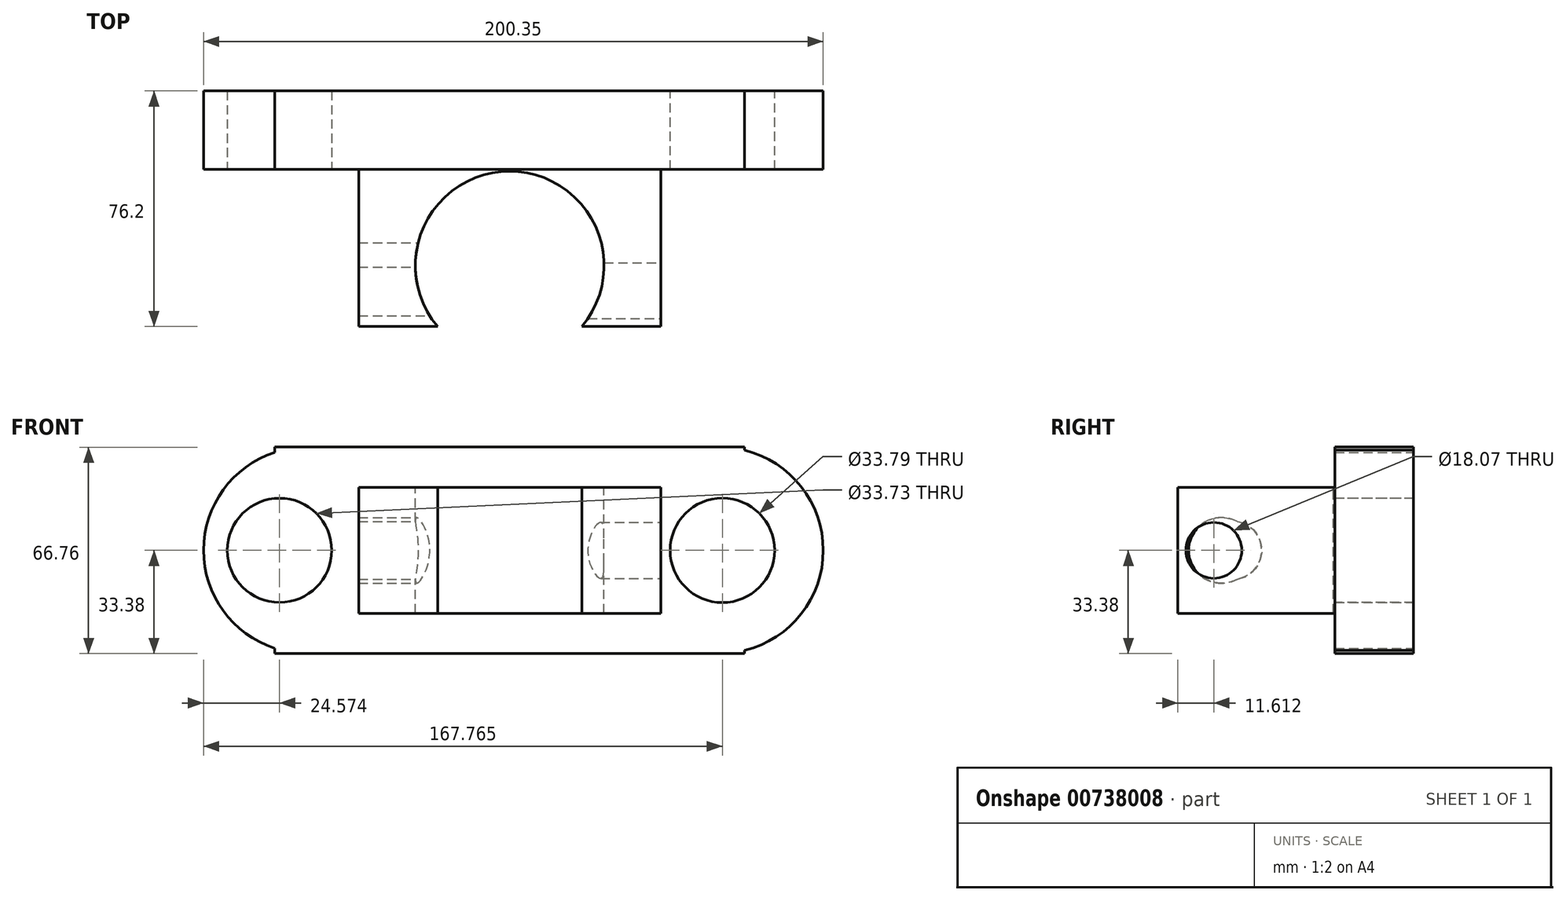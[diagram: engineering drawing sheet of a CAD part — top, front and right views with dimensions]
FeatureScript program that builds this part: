
annotation { "Feature Type Name" : "Feature", "Feature Type Description" : "" }
export const myFeature = defineFeature(function(context is Context, id is Id, definition is map)
    precondition{}
    {
        {
            var Q0;
            Q0=qCreatedBy(makeId("Front.planeOp"),FACE);
            var sketch = newSketch(context, id + "F0", { "sketchPlane" : qUnion([Q0])});
            skLineSegment(sketch, "E0.bottom", {"start": v(-75.97, 33.38) * mm, "end": v(75.97, 33.38) * mm});
            skLineSegment(sketch, "E0.top", {"start": v(-75.97, -33.38) * mm, "end": v(75.97, -33.38) * mm});
            skLineSegment(sketch, "E0.left", {"start": v(-75.97, 33.38) * mm, "end": v(-75.97, 31.65) * mm});
            skLineSegment(sketch, "E0.right", {"start": v(75.97, 33.38) * mm, "end": v(75.97, 32.37) * mm});
            skPoint(sketch, "E0.middle", {"position": v(0, 0) * mm});
            skArc(sketch, "E1", {"start": v(75.97, -32.37) * mm, "mid": v(101.36, 0) * mm, "end": v(75.97, 32.37) * mm});
            skArc(sketch, "E2", {"start": v(-75.97, 31.65) * mm, "mid": v(-99, 0) * mm, "end": v(-75.97, -31.65) * mm});
            skLineSegment(sketch, "E3.trimOffspring", {"start": v(-75.97, -31.65) * mm, "end": v(-75.97, -33.38) * mm});
            skLineSegment(sketch, "E4.trimOffspring", {"start": v(75.97, -32.37) * mm, "end": v(75.97, -33.38) * mm});
            skSolve(sketch);
        }
        {
            var Q0;
            Q0=makeQuery(id+"F0.imprint","IMPRINT",FACE,{"disambiguationData":[TD([[makeQuery(id+"F0.imprint","IMPRINT",EDGE,{"derivedFrom":sQuery(id+"F0.wireOp",EDGE,"E0.bottom")}),-1.0]])]});
            var sketch = newSketch(context, id + "F1", { "sketchPlane" : qUnion([Q0])});
            skSolve(sketch);
        }
        {
            var Q0;
            Q0=makeQuery(id+"F1.imprint","IMPRINT",FACE,{"disambiguationData":[TD([[makeQuery(id+"F1.imprint","IMPRINT",EDGE,{"derivedFrom":makeQuery(id+"F0.imprint","IMPRINT",EDGE,{"derivedFrom":sQuery(id+"F0.wireOp",EDGE,"E0.bottom")})}),-1.0]])]});
            extrude(context, id + "F2", {"entities" : qUnion([Q0]), "depth" : 25.4 * mm, "offsetDistance" : 25.4 * mm});
        }
        {
            var Q0;
            Q0=qCreatedBy(makeId("Front.planeOp"),FACE);
            var sketch = newSketch(context, id + "F3", { "sketchPlane" : qUnion([Q0])});
            skCircle(sketch, "E5", {"center": v(-75.37, 0) * mm, "radius": 14.29 * mm});
            skCircle(sketch, "E6", {"center": v(76.27, 0) * mm, "radius": 15.04 * mm});
            skSolve(sketch);
        }
        {
            var Q0;
            Q0 = qSketchRegion(id + "F3", true);
            extrude(context, id + "F4", {"entities" : qUnion([Q0]), "operationType" : NewBodyOperationType.REMOVE, "oppositeDirection" : true, "depth" : 25.4 * mm, "offsetDistance" : 25.4 * mm});
        }
        {
            var Q0;
            Q0=qCreatedBy(makeId("Front.planeOp"),FACE);
            var sketch = newSketch(context, id + "F5", { "sketchPlane" : qUnion([Q0])});
            skCircle(sketch, "E7", {"center": v(74.6, 0) * mm, "radius": 15.1 * mm});
            skSolve(sketch);
        }
        {
            var Q0;
            Q0 = qSketchRegion(id + "F5", true);
            extrude(context, id + "F6", {"entities" : qUnion([Q0]), "operationType" : NewBodyOperationType.REMOVE, "oppositeDirection" : true, "depth" : 25.4 * mm, "offsetDistance" : 25.4 * mm});
        }
        {
            var Q0;
            Q0=qCreatedBy(makeId("Front.planeOp"),FACE);
            var sketch = newSketch(context, id + "F7", { "sketchPlane" : qUnion([Q0])});
            skCircle(sketch, "E8", {"center": v(68.77, 0) * mm, "radius": 16.9 * mm});
            skSolve(sketch);
        }
        {
            var Q0;
            Q0 = qSketchRegion(id + "F7", true);
            extrude(context, id + "F8", {"entities" : qUnion([Q0]), "operationType" : NewBodyOperationType.REMOVE, "depth" : 25.4 * mm, "offsetDistance" : 25.4 * mm, "symmetric" : true});
        }
        {
            var Q0;
            Q0 = qSketchRegion(id + "F0", true);
            extrude(context, id + "F9", {"entities" : qUnion([Q0]), "operationType" : NewBodyOperationType.REMOVE, "oppositeDirection" : true, "depth" : 25.4 * mm, "offsetDistance" : 25.4 * mm});
        }
        {
            var Q0;
            Q0=qCreatedBy(makeId("Front.planeOp"),FACE);
            var sketch = newSketch(context, id + "F10", { "sketchPlane" : qUnion([Q0])});
            skCircle(sketch, "E9", {"center": v(-71, 0) * mm, "radius": 15.35 * mm});
            skSolve(sketch);
        }
        {
            var Q0;
            Q0 = qSketchRegion(id + "F10", true);
            extrude(context, id + "F11", {"entities" : qUnion([Q0]), "operationType" : NewBodyOperationType.REMOVE, "oppositeDirection" : true, "depth" : 76.2 * mm, "offsetDistance" : 25.4 * mm});
        }
        {
            var Q0;
            Q0=makeQuery(id+"F8.boolean.opBoolean","COPY",FACE,{"derivedFrom":makeQuery(id+"F8.opExtrude","CAP_FACE",FACE,{"disambiguationData":[OSD([sQuery(id+"F7.wireOp",EDGE,"E8")])],"isStart":false})});
            extrude(context, id + "F12", {"entities" : qUnion([Q0]), "operationType" : NewBodyOperationType.REMOVE, "oppositeDirection" : true, "depth" : 25.4 * mm, "offsetDistance" : 25.4 * mm});
        }
        {
            var Q0;
            Q0=makeQuery(id+"F2.opExtrude","CAP_FACE",FACE,{"disambiguationData":[OSD([sQuery(id+"F0.wireOp",EDGE,"E0.bottom"),sQuery(id+"F0.wireOp",EDGE,"E0.top"),sQuery(id+"F0.wireOp",EDGE,"E0.left"),sQuery(id+"F0.wireOp",EDGE,"E0.right"),sQuery(id+"F0.wireOp",EDGE,"E1"),sQuery(id+"F0.wireOp",EDGE,"E2"),sQuery(id+"F0.wireOp",EDGE,"E3.trimOffspring"),sQuery(id+"F0.wireOp",EDGE,"E4.trimOffspring")])],"isStart":false});
            var sketch = newSketch(context, id + "F13", { "sketchPlane" : qUnion([Q0])});
            skCircle(sketch, "E10", {"center": v(-74.42, 0) * mm, "radius": 16.87 * mm});
            skSolve(sketch);
        }
        {
            var Q0;
            Q0=makeQuery(id+"F13.imprint","IMPRINT",FACE,{"disambiguationData":[TD([[makeQuery(id+"F13.imprint","IMPRINT",EDGE,{"derivedFrom":sQuery(id+"F13.wireOp",EDGE,"E10")}),1.0]])]});
            extrude(context, id + "F14", {"entities" : qUnion([Q0]), "operationType" : NewBodyOperationType.REMOVE, "oppositeDirection" : true, "depth" : 25.4 * mm, "offsetDistance" : 25.4 * mm});
        }
        {
            var Q0;
            Q0=qCreatedBy(makeId("Front.planeOp"),FACE);
            var sketch = newSketch(context, id + "F15", { "sketchPlane" : qUnion([Q0])});
            skLineSegment(sketch, "E11.bottom", {"start": v(-48.83, 20.36) * mm, "end": v(48.83, 20.36) * mm});
            skLineSegment(sketch, "E11.top", {"start": v(-48.83, -20.36) * mm, "end": v(48.83, -20.36) * mm});
            skLineSegment(sketch, "E11.left", {"start": v(-48.83, 20.36) * mm, "end": v(-48.83, -20.36) * mm});
            skLineSegment(sketch, "E11.right", {"start": v(48.83, 20.36) * mm, "end": v(48.83, -20.36) * mm});
            skPoint(sketch, "E11.middle", {"position": v(0, 0) * mm});
            skSolve(sketch);
        }
        {
            var Q0;
            Q0 = qSketchRegion(id + "F15", true);
            extrude(context, id + "F16", {"entities" : qUnion([Q0]), "operationType" : NewBodyOperationType.ADD, "depth" : 76.2 * mm, "offsetDistance" : 25.4 * mm});
        }
        {
            var Q0;
            Q0=qCreatedBy(makeId("Top.planeOp"),FACE);
            var sketch = newSketch(context, id + "F17", { "sketchPlane" : qUnion([Q0])});
            skCircle(sketch, "E12", {"center": v(0, -56.5) * mm, "radius": 30.52 * mm});
            skSolve(sketch);
        }
        {
            var Q0;
            Q0 = qSketchRegion(id + "F17", true);
            extrude(context, id + "F18", {"entities" : qUnion([Q0]), "operationType" : NewBodyOperationType.REMOVE, "oppositeDirection" : true, "depth" : 25.4 * mm, "offsetDistance" : 25.4 * mm});
        }
        {
            var Q0;
            Q0=makeQuery(id+"F18.boolean.opBoolean","COPY",FACE,{"derivedFrom":makeQuery(id+"F18.opExtrude","CAP_FACE",FACE,{"disambiguationData":[OSD([sQuery(id+"F17.wireOp",EDGE,"E12")])],"isStart":true})});
            extrude(context, id + "F19", {"entities" : qUnion([Q0]), "operationType" : NewBodyOperationType.REMOVE, "oppositeDirection" : true, "depth" : 25.4 * mm, "offsetDistance" : 25.4 * mm});
        }
        {
            var Q0;
            Q0=qCreatedBy(makeId("Right.planeOp"),FACE);
            var sketch = newSketch(context, id + "F20", { "sketchPlane" : qUnion([Q0])});
            skCircle(sketch, "E13", {"center": v(-62.1, 0) * mm, "radius": 10.62 * mm});
            skSolve(sketch);
        }
        {
            var Q0;
            Q0 = qSketchRegion(id + "F20", true);
            extrude(context, id + "F21", {"entities" : qUnion([Q0]), "operationType" : NewBodyOperationType.REMOVE, "oppositeDirection" : true, "depth" : 50.8 * mm, "offsetDistance" : 25.4 * mm});
        }
        {
            var Q0;
            Q0=qCreatedBy(makeId("Right.planeOp"),FACE);
            var sketch = newSketch(context, id + "F22", { "sketchPlane" : qUnion([Q0])});
            skCircle(sketch, "E14", {"center": v(-58.52, 0) * mm, "radius": 9.42 * mm});
            skSolve(sketch);
        }
        {
            var Q0;
            Q0 = qSketchRegion(id + "F22", true);
            extrude(context, id + "F23", {"entities" : qUnion([Q0]), "operationType" : NewBodyOperationType.REMOVE, "oppositeDirection" : true, "depth" : 50.8 * mm, "offsetDistance" : 25.4 * mm});
        }
        {
            var Q0;
            Q0=makeQuery(id+"F16.opExtrude","SWEPT_FACE",FACE,{"disambiguationData":[OSD([sQuery(id+"F15.wireOp",EDGE,"E11.right")])]});
            var sketch = newSketch(context, id + "F24", { "sketchPlane" : qUnion([Q0])});
            skCircle(sketch, "E15", {"center": v(-64.59, 0) * mm, "radius": 9.04 * mm});
            skSolve(sketch);
        }
        {
            var Q0;
            Q0 = qSketchRegion(id + "F24", true);
            extrude(context, id + "F25", {"entities" : qUnion([Q0]), "operationType" : NewBodyOperationType.REMOVE, "oppositeDirection" : true, "depth" : 25.4 * mm, "offsetDistance" : 25.4 * mm});
        }
    });
